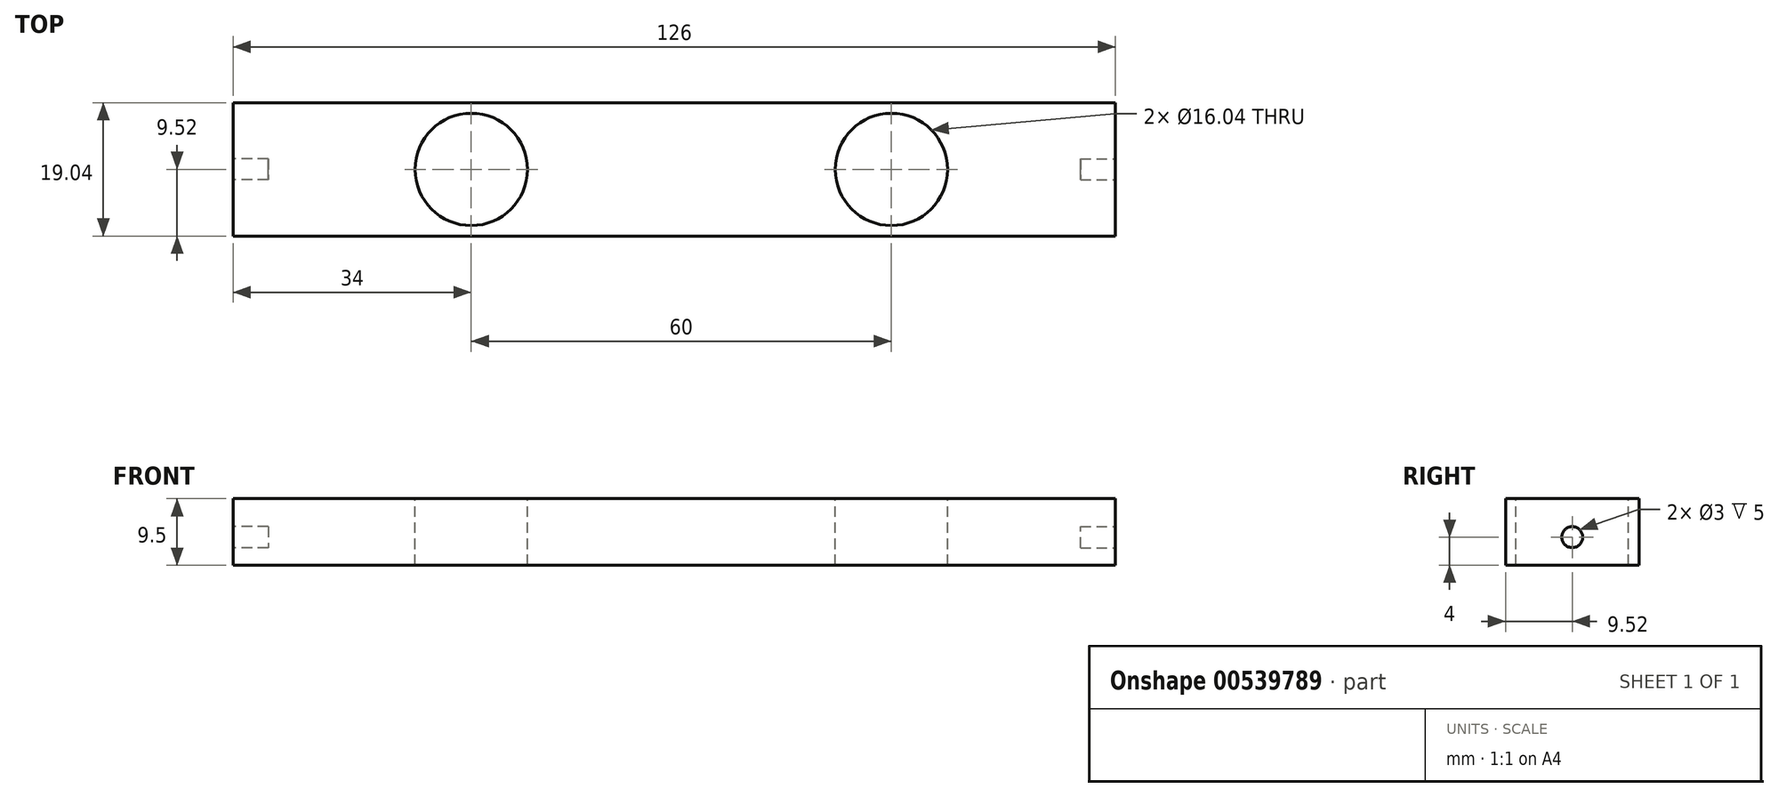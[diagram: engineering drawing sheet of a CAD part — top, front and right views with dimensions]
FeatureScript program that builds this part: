
annotation { "Feature Type Name" : "Feature", "Feature Type Description" : "" }
export const myFeature = defineFeature(function(context is Context, id is Id, definition is map)
    precondition{}
    {
        {
            var Q0;
            Q0=qCreatedBy(makeId("Top.planeOp"),FACE);
            var sketch = newSketch(context, id + "F0", { "sketchPlane" : qUnion([Q0])});
            skLineSegment(sketch, "E0.bottom", {"start": v(63, 9.52) * mm, "end": v(-63, 9.52) * mm});
            skLineSegment(sketch, "E0.top", {"start": v(63, -9.52) * mm, "end": v(-63, -9.52) * mm});
            skLineSegment(sketch, "E0.left", {"start": v(63, 9.52) * mm, "end": v(63, -9.52) * mm});
            skLineSegment(sketch, "E0.right", {"start": v(-63, 9.52) * mm, "end": v(-63, -9.52) * mm});
            skPoint(sketch, "E0.middle", {"position": v(0, 0) * mm});
            skSolve(sketch);
        }
        {
            var Q0;
            Q0 = qSketchRegion(id + "F0", true);
            extrude(context, id + "F1", {"entities" : qUnion([Q0]), "depth" : 9.5 * mm, "offsetDistance" : 25 * mm});
        }
        {
            var Q0;
            Q0=makeQuery(id+"F1.opExtrude","SWEPT_FACE",FACE,{"disambiguationData":[OSD([sQuery(id+"F0.wireOp",EDGE,"E0.left")])]});
            var sketch = newSketch(context, id + "F2", { "sketchPlane" : qUnion([Q0])});
            skCircle(sketch, "E1", {"center": v(0, 4) * mm, "radius": 1.5 * mm});
            skSolve(sketch);
        }
        {
            var Q0;
            Q0 = qSketchRegion(id + "F2", true);
            extrude(context, id + "F3", {"entities" : qUnion([Q0]), "operationType" : NewBodyOperationType.REMOVE, "oppositeDirection" : true, "depth" : 5 * mm, "offsetDistance" : 25 * mm});
        }
        {
            var Q0;
            Q0=makeQuery(id+"F1.opExtrude","SWEPT_FACE",FACE,{"disambiguationData":[OSD([sQuery(id+"F0.wireOp",EDGE,"E0.right")])]});
            var sketch = newSketch(context, id + "F4", { "sketchPlane" : qUnion([Q0])});
            skCircle(sketch, "E2", {"center": v(0, 4) * mm, "radius": 1.5 * mm});
            skSolve(sketch);
        }
        {
            var Q0;
            Q0 = qSketchRegion(id + "F4", true);
            extrude(context, id + "F5", {"entities" : qUnion([Q0]), "operationType" : NewBodyOperationType.REMOVE, "oppositeDirection" : true, "depth" : 5 * mm, "offsetDistance" : 25 * mm});
        }
        {
            var Q0;
            Q0=makeQuery(id+"F1.opExtrude","CAP_FACE",FACE,{"disambiguationData":[OSD([sQuery(id+"F0.wireOp",EDGE,"E0.bottom"),sQuery(id+"F0.wireOp",EDGE,"E0.top"),sQuery(id+"F0.wireOp",EDGE,"E0.left"),sQuery(id+"F0.wireOp",EDGE,"E0.right")])],"isStart":false});
            var sketch = newSketch(context, id + "F6", { "sketchPlane" : qUnion([Q0])});
            skCircle(sketch, "E3", {"center": v(-29, 0) * mm, "radius": 8.02 * mm});
            skPoint(sketch, "E3.centerSnap0", {"position": v(-63, 0) * mm});
            skCircle(sketch, "E4", {"center": v(31, 0) * mm, "radius": 8.02 * mm});
            skSolve(sketch);
        }
        {
            var Q0;
            Q0 = qSketchRegion(id + "F6", true);
            extrude(context, id + "F7", {"entities" : qUnion([Q0]), "operationType" : NewBodyOperationType.REMOVE, "oppositeDirection" : true, "depth" : 9.5 * mm, "offsetDistance" : 25 * mm});
        }
    });
